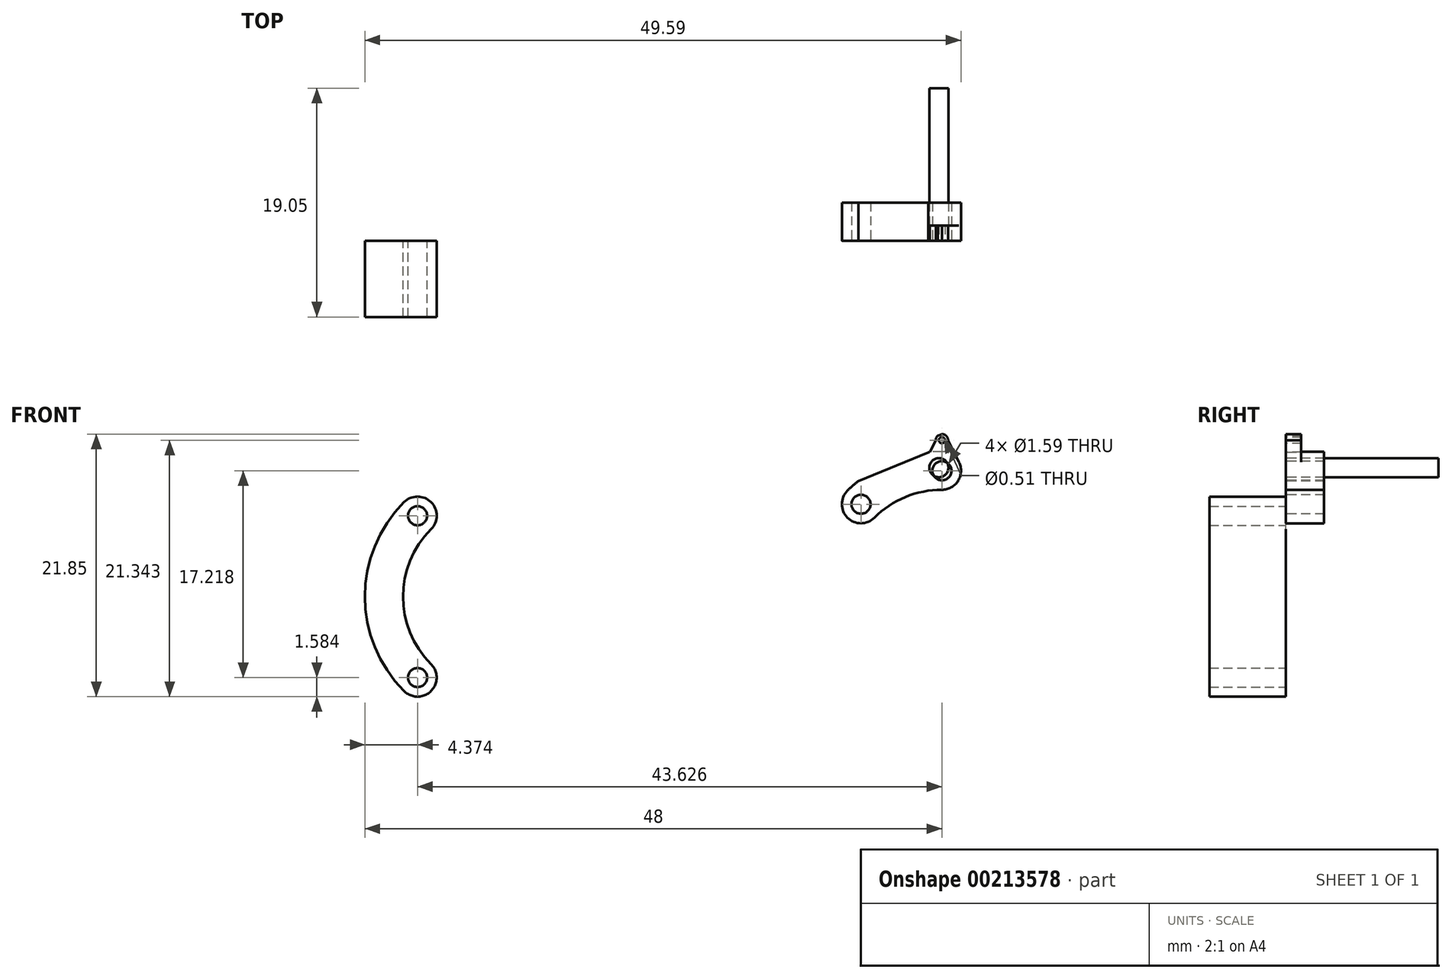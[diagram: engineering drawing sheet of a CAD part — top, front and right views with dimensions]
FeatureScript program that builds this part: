
annotation { "Feature Type Name" : "Feature", "Feature Type Description" : "" }
export const myFeature = defineFeature(function(context is Context, id is Id, definition is map)
    precondition{}
    {
        {
            var Q0;
            Q0=qCreatedBy(makeId("Front.planeOp"),FACE);
            var sketch = newSketch(context, id + "F0", { "sketchPlane" : qUnion([Q0])});
            skCircle(sketch, "E0", {"center": v(0, 0) * mm, "radius": 7.94 * mm});
            skCircle(sketch, "E1", {"center": v(0, 0) * mm, "radius": 11.11 * mm});
            skCircle(sketch, "E2", {"center": v(0, 0) * mm, "radius": 9.53 * mm, "construction": true});
            skLineSegment(sketch, "E3", {"start": v(0, 14.42) * mm, "end": v(0, -15.59) * mm, "construction": true});
            skLineSegment(sketch, "E4", {"start": v(-14.56, 0) * mm, "end": v(14.44, 0) * mm, "construction": true});
            skLineSegment(sketch, "E5", {"start": v(0, 0) * mm, "end": v(10.85, 10.85) * mm, "construction": true});
            skLineSegment(sketch, "E6", {"start": v(0, 0) * mm, "end": v(-10.67, -10.67) * mm, "construction": true});
            skLineSegment(sketch, "E7", {"start": v(0, 0) * mm, "end": v(-10.13, 10.13) * mm, "construction": true});
            skLineSegment(sketch, "E8", {"start": v(0, 0) * mm, "end": v(10, -10) * mm, "construction": true});
            skCircle(sketch, "E9", {"center": v(0, 9.53) * mm, "radius": 0.8 * mm});
            skCircle(sketch, "E10", {"center": v(-6.74, 6.74) * mm, "radius": 0.8 * mm});
            skCircle(sketch, "E11", {"center": v(-6.74, -6.74) * mm, "radius": 0.8 * mm});
            skCircle(sketch, "E12", {"center": v(6.74, -6.74) * mm, "radius": 0.8 * mm});
            skCircle(sketch, "E13", {"center": v(6.74, 6.74) * mm, "radius": 0.8 * mm});
            skCircle(sketch, "E14", {"center": v(0, -9.53) * mm, "radius": 0.8 * mm});
            skCircle(sketch, "E15", {"center": v(0, 9.53) * mm, "radius": 1.59 * mm});
            skCircle(sketch, "E16", {"center": v(-6.74, 6.74) * mm, "radius": 1.59 * mm});
            skCircle(sketch, "E17", {"center": v(-6.74, -6.74) * mm, "radius": 1.59 * mm});
            skCircle(sketch, "E18", {"center": v(0, -9.53) * mm, "radius": 1.59 * mm});
            skCircle(sketch, "E19", {"center": v(6.74, -6.74) * mm, "radius": 1.59 * mm});
            skCircle(sketch, "E20", {"center": v(6.74, 6.74) * mm, "radius": 1.59 * mm});
            skCircle(sketch, "E21", {"center": v(0, 12.07) * mm, "radius": 0.25 * mm});
            skCircle(sketch, "E22", {"center": v(-8.53, 8.53) * mm, "radius": 0.25 * mm});
            skCircle(sketch, "E23", {"center": v(-8.53, -8.53) * mm, "radius": 0.25 * mm});
            skCircle(sketch, "E24", {"center": v(0, -12.07) * mm, "radius": 0.25 * mm});
            skCircle(sketch, "E25", {"center": v(8.53, -8.53) * mm, "radius": 0.25 * mm});
            skCircle(sketch, "E26", {"center": v(8.53, 8.53) * mm, "radius": 0.25 * mm});
            skCircle(sketch, "E27", {"center": v(0, 12.07) * mm, "radius": 0.5 * mm});
            skCircle(sketch, "E28", {"center": v(-8.53, 8.53) * mm, "radius": 0.5 * mm});
            skCircle(sketch, "E29", {"center": v(8.53, 8.53) * mm, "radius": 0.5 * mm});
            skCircle(sketch, "E30", {"center": v(8.53, -8.53) * mm, "radius": 0.5 * mm});
            skCircle(sketch, "E31", {"center": v(0, -12.07) * mm, "radius": 0.5 * mm});
            skCircle(sketch, "E32", {"center": v(-8.53, -8.53) * mm, "radius": 0.5 * mm});
            skLineSegment(sketch, "E33", {"start": v(-0.5, 12.05) * mm, "end": v(-1.42, 10.24) * mm});
            skLineSegment(sketch, "E34", {"start": v(0.5, 12.05) * mm, "end": v(1.42, 10.24) * mm});
            skLineSegment(sketch, "E35", {"start": v(-8.88, 8.16) * mm, "end": v(-8.24, 6.23) * mm});
            skLineSegment(sketch, "E36", {"start": v(-8.16, 8.88) * mm, "end": v(-6.23, 8.24) * mm});
            skLineSegment(sketch, "E37", {"start": v(-8.88, -8.16) * mm, "end": v(-8.24, -6.23) * mm});
            skLineSegment(sketch, "E38", {"start": v(-8.16, -8.88) * mm, "end": v(-6.23, -8.24) * mm});
            skLineSegment(sketch, "E39", {"start": v(-0.5, -12.05) * mm, "end": v(-1.42, -10.24) * mm});
            skLineSegment(sketch, "E40", {"start": v(0.5, -12.05) * mm, "end": v(1.42, -10.24) * mm});
            skLineSegment(sketch, "E41", {"start": v(8.16, -8.88) * mm, "end": v(6.23, -8.24) * mm});
            skLineSegment(sketch, "E42", {"start": v(8.88, -8.16) * mm, "end": v(8.24, -6.23) * mm});
            skLineSegment(sketch, "E43", {"start": v(8.88, 8.16) * mm, "end": v(8.24, 6.23) * mm});
            skLineSegment(sketch, "E44", {"start": v(8.16, 8.88) * mm, "end": v(6.23, 8.24) * mm});
            skLineSegment(sketch, "E45", {"start": v(-8.17, 8.17) * mm, "end": v(0, 11.52) * mm});
            skLineSegment(sketch, "E46", {"start": v(0, 12.57) * mm, "end": v(-8.92, 8.92) * mm});
            skLineSegment(sketch, "E47", {"start": v(-8.92, 8.92) * mm, "end": v(-8.9, -8.9) * mm});
            skLineSegment(sketch, "E48", {"start": v(-8.17, 8.17) * mm, "end": v(-8.17, -8.17) * mm});
            skLineSegment(sketch, "E49", {"start": v(0, -12.57) * mm, "end": v(-8.9, -8.9) * mm});
            skLineSegment(sketch, "E50", {"start": v(0, -11.56) * mm, "end": v(-8.17, -8.17) * mm});
            skSolve(sketch);
        }
        {
            var Q0;
            Q0=qCreatedBy(makeId("Front.planeOp"),FACE);
            var sketch = newSketch(context, id + "F1", { "sketchPlane" : qUnion([Q0])});
            skCircle(sketch, "E51", {"center": v(0.25, -0.25) * mm, "radius": 7.94 * mm});
            skCircle(sketch, "E52", {"center": v(0.25, -0.25) * mm, "radius": 11.11 * mm});
            skCircle(sketch, "E53", {"center": v(0.25, -0.25) * mm, "radius": 9.53 * mm, "construction": true});
            skLineSegment(sketch, "E54", {"start": v(0.25, 14.16) * mm, "end": v(0.25, -15.84) * mm, "construction": true});
            skLineSegment(sketch, "E55", {"start": v(-14.31, -0.25) * mm, "end": v(14.69, -0.25) * mm, "construction": true});
            skLineSegment(sketch, "E56", {"start": v(0.25, -0.25) * mm, "end": v(11.1, 10.6) * mm, "construction": true});
            skLineSegment(sketch, "E57", {"start": v(0.25, -0.25) * mm, "end": v(-10.42, -10.93) * mm, "construction": true});
            skLineSegment(sketch, "E58", {"start": v(0.25, -0.25) * mm, "end": v(-9.88, 9.88) * mm, "construction": true});
            skLineSegment(sketch, "E59", {"start": v(0.25, -0.25) * mm, "end": v(10.24, -10.25) * mm, "construction": true});
            skCircle(sketch, "E60", {"center": v(0.25, 9.27) * mm, "radius": 0.8 * mm});
            skCircle(sketch, "E61", {"center": v(-6.49, 6.48) * mm, "radius": 0.8 * mm});
            skCircle(sketch, "E62", {"center": v(-6.49, -6.99) * mm, "radius": 0.8 * mm});
            skCircle(sketch, "E63", {"center": v(6.98, -6.99) * mm, "radius": 0.8 * mm});
            skCircle(sketch, "E64", {"center": v(6.98, 6.48) * mm, "radius": 0.8 * mm});
            skCircle(sketch, "E65", {"center": v(0.25, -9.78) * mm, "radius": 0.8 * mm});
            skCircle(sketch, "E66", {"center": v(0.25, 9.27) * mm, "radius": 1.59 * mm});
            skCircle(sketch, "E67", {"center": v(-6.49, 6.48) * mm, "radius": 1.59 * mm});
            skCircle(sketch, "E68", {"center": v(-6.49, -6.99) * mm, "radius": 1.59 * mm});
            skCircle(sketch, "E69", {"center": v(0.25, -9.78) * mm, "radius": 1.59 * mm});
            skCircle(sketch, "E70", {"center": v(6.98, -6.99) * mm, "radius": 1.59 * mm});
            skCircle(sketch, "E71", {"center": v(6.98, 6.48) * mm, "radius": 1.59 * mm});
            skCircle(sketch, "E72", {"center": v(0.25, 11.81) * mm, "radius": 0.25 * mm});
            skCircle(sketch, "E73", {"center": v(-8.28, 8.28) * mm, "radius": 0.25 * mm});
            skCircle(sketch, "E74", {"center": v(-8.28, -8.78) * mm, "radius": 0.25 * mm});
            skCircle(sketch, "E75", {"center": v(0.25, -12.32) * mm, "radius": 0.25 * mm});
            skCircle(sketch, "E76", {"center": v(8.78, -8.78) * mm, "radius": 0.25 * mm});
            skCircle(sketch, "E77", {"center": v(8.78, 8.28) * mm, "radius": 0.25 * mm});
            skCircle(sketch, "E78", {"center": v(0.25, 11.81) * mm, "radius": 0.5 * mm});
            skCircle(sketch, "E79", {"center": v(-8.28, 8.28) * mm, "radius": 0.5 * mm});
            skCircle(sketch, "E80", {"center": v(8.78, 8.28) * mm, "radius": 0.5 * mm});
            skCircle(sketch, "E81", {"center": v(8.78, -8.78) * mm, "radius": 0.5 * mm});
            skCircle(sketch, "E82", {"center": v(0.25, -12.32) * mm, "radius": 0.5 * mm});
            skCircle(sketch, "E83", {"center": v(-8.28, -8.78) * mm, "radius": 0.5 * mm});
            skLineSegment(sketch, "E84", {"start": v(-0.26, 11.8) * mm, "end": v(-1.17, 9.98) * mm});
            skLineSegment(sketch, "E85", {"start": v(0.76, 11.8) * mm, "end": v(1.67, 9.98) * mm});
            skLineSegment(sketch, "E86", {"start": v(-8.63, 7.91) * mm, "end": v(-8, 5.98) * mm});
            skLineSegment(sketch, "E87", {"start": v(-7.91, 8.63) * mm, "end": v(-5.99, 7.99) * mm});
            skLineSegment(sketch, "E88", {"start": v(-8.63, -8.42) * mm, "end": v(-8, -6.49) * mm});
            skLineSegment(sketch, "E89", {"start": v(-7.91, -9.14) * mm, "end": v(-5.99, -8.5) * mm});
            skLineSegment(sketch, "E90", {"start": v(-0.26, -12.3) * mm, "end": v(-1.17, -10.49) * mm});
            skLineSegment(sketch, "E91", {"start": v(0.76, -12.3) * mm, "end": v(1.67, -10.49) * mm});
            skLineSegment(sketch, "E92", {"start": v(8.41, -9.14) * mm, "end": v(6.48, -8.5) * mm});
            skLineSegment(sketch, "E93", {"start": v(9.13, -8.42) * mm, "end": v(8.5, -6.49) * mm});
            skLineSegment(sketch, "E94", {"start": v(9.13, 7.91) * mm, "end": v(8.5, 5.98) * mm});
            skLineSegment(sketch, "E95", {"start": v(8.41, 8.63) * mm, "end": v(6.48, 7.99) * mm});
            skLineSegment(sketch, "E96", {"start": v(-7.92, 7.92) * mm, "end": v(0.25, 11.26) * mm});
            skLineSegment(sketch, "E97", {"start": v(0.25, 12.32) * mm, "end": v(-8.67, 8.67) * mm});
            skLineSegment(sketch, "E98", {"start": v(-8.67, 8.67) * mm, "end": v(-8.64, -9.14) * mm});
            skLineSegment(sketch, "E99", {"start": v(-7.92, 7.92) * mm, "end": v(-7.92, -8.42) * mm});
            skLineSegment(sketch, "E100", {"start": v(0.25, -12.83) * mm, "end": v(-8.64, -9.14) * mm});
            skLineSegment(sketch, "E101", {"start": v(0.25, -11.8) * mm, "end": v(-7.92, -8.42) * mm});
            skSolve(sketch);
        }
        {
            var Q0;
            Q0=makeQuery(id+"F0.imprint","IMPRINT",FACE,{"disambiguationData":[TD([[makeQuery(id+"F0.imprint","IMPRINT",EDGE,{"derivedFrom":sQuery(id+"F0.wireOp",EDGE,"E9")}),1.0]])]});
            extrude(context, id + "F2", {"entities" : qUnion([Q0]), "oppositeDirection" : true, "depth" : 12.7 * mm});
        }
        {
            var Q0;
            Q0=makeQuery(id+"F1.imprint","IMPRINT",FACE,{"disambiguationData":[TD([[makeQuery(id+"F1.imprint","IMPRINT",EDGE,{"derivedFrom":sQuery(id+"F1.wireOp",EDGE,"E60")}),-1.0]])]});
            var Q1;
            {var subQ1=sQuery(id+"F1.wireOp",EDGE,"E66");var subQ3=sQuery(id+"F1.wireOp",EDGE,"E51");var subQ4=makeQuery(id+"F1.imprint","INTERSECT",VERTEX,{"derivedFrom":[subQ3,subQ1]});Q1=makeQuery(id+"F1.imprint","IMPRINT",FACE,{"disambiguationData":[TD([[makeQuery(id+"F1.imprint","IMPRINT",EDGE,{"disambiguationData":[TD([[subQ4,-1.0]])],"derivedFrom":subQ3}),-1.0]])]});}
            var Q2;
            {var subQ0=sQuery(id+"F1.wireOp",EDGE,"E66");var subQ1=sQuery(id+"F1.wireOp",EDGE,"E52");var subQ2=makeQuery(id+"F1.imprint","INTERSECT",VERTEX,{"derivedFrom":[subQ1,subQ0]});Q2=makeQuery(id+"F1.imprint","IMPRINT",FACE,{"disambiguationData":[TD([[makeQuery(id+"F1.imprint","IMPRINT",EDGE,{"disambiguationData":[TD([[subQ2,-1.0]])],"derivedFrom":subQ1}),1.0]])]});}
            var Q3;
            {var subQ0=sQuery(id+"F1.wireOp",EDGE,"E87");var subQ1=sQuery(id+"F1.wireOp",EDGE,"E52");var subQ2=makeQuery(id+"F1.imprint","INTERSECT",VERTEX,{"derivedFrom":[subQ1,subQ0]});Q3=makeQuery(id+"F1.imprint","IMPRINT",FACE,{"disambiguationData":[TD([[makeQuery(id+"F1.imprint","IMPRINT",EDGE,{"disambiguationData":[TD([[subQ2,-1.0]])],"derivedFrom":subQ1}),1.0]])]});}
            var Q4;
            Q4=makeQuery(id+"F1.imprint","IMPRINT",FACE,{"disambiguationData":[TD([[makeQuery(id+"F1.imprint","IMPRINT",EDGE,{"derivedFrom":sQuery(id+"F1.wireOp",EDGE,"E61")}),-1.0]])]});
            var Q5;
            {var subQ0=sQuery(id+"F1.wireOp",EDGE,"E67");var subQ1=makeQuery(id+"F1.imprint","INTERSECT",VERTEX,{"derivedFrom":[subQ0,sQuery(id+"F1.wireOp",EDGE,"E86")]});Q5=makeQuery(id+"F1.imprint","IMPRINT",FACE,{"disambiguationData":[TD([[makeQuery(id+"F1.imprint","IMPRINT",EDGE,{"disambiguationData":[TD([[subQ1,1.0]])],"derivedFrom":subQ0}),1.0]])]});}
            var Q6;
            {var subQ0=sQuery(id+"F1.wireOp",EDGE,"E96");var subQ1=sQuery(id+"F1.wireOp",EDGE,"E52");var subQ2=makeQuery(id+"F1.imprint","INTERSECT",VERTEX,{"disambiguationData":[OD(0.0)],"derivedFrom":[subQ1,subQ0]});Q6=makeQuery(id+"F1.imprint","IMPRINT",FACE,{"disambiguationData":[TD([[makeQuery(id+"F1.imprint","IMPRINT",EDGE,{"disambiguationData":[TD([[subQ2,-1.0]])],"derivedFrom":subQ1}),1.0]])]});}
            extrude(context, id + "F3", {"entities" : qUnion([Q0, Q1, Q2, Q3, Q4, Q5, Q6]), "oppositeDirection" : true, "depth" : 3.17 * mm});
        }
        {
            var Q0;
            {var subQ4=sQuery(id+"F1.wireOp",EDGE,"E85");var subQ5=sQuery(id+"F1.wireOp",EDGE,"E52");var subQ6=makeQuery(id+"F1.imprint","INTERSECT",VERTEX,{"derivedFrom":[subQ5,subQ4]});Q0=makeQuery(id+"F1.imprint","IMPRINT",FACE,{"disambiguationData":[TD([[makeQuery(id+"F1.imprint","IMPRINT",EDGE,{"disambiguationData":[TD([[subQ6,-1.0]])],"derivedFrom":subQ5}),-1.0]])]});}
            var Q1;
            Q1=makeQuery(id+"F1.imprint","IMPRINT",FACE,{"disambiguationData":[TD([[makeQuery(id+"F1.imprint","IMPRINT",EDGE,{"derivedFrom":sQuery(id+"F1.wireOp",EDGE,"E72")}),-1.0]])]});
            var Q2;
            {var subQ0=sQuery(id+"F1.wireOp",EDGE,"E85");var subQ1=sQuery(id+"F1.wireOp",EDGE,"E52");var subQ2=makeQuery(id+"F1.imprint","INTERSECT",VERTEX,{"derivedFrom":[subQ1,subQ0]});Q2=makeQuery(id+"F1.imprint","IMPRINT",FACE,{"disambiguationData":[TD([[makeQuery(id+"F1.imprint","IMPRINT",EDGE,{"disambiguationData":[TD([[subQ2,-1.0]])],"derivedFrom":subQ1}),1.0]])]});}
            var Q3;
            {var subQ0=sQuery(id+"F1.wireOp",EDGE,"E97");var subQ1=sQuery(id+"F1.wireOp",EDGE,"E78");var subQ2=makeQuery(id+"F1.imprint","INTERSECT",VERTEX,{"disambiguationData":[OD(0.0)],"derivedFrom":[subQ1,subQ0]});Q3=makeQuery(id+"F1.imprint","IMPRINT",FACE,{"disambiguationData":[TD([[makeQuery(id+"F1.imprint","IMPRINT",EDGE,{"disambiguationData":[TD([[subQ2,-1.0]])],"derivedFrom":subQ1}),1.0]])]});}
            extrude(context, id + "F4", {"entities" : qUnion([Q0, Q1, Q2, Q3]), "operationType" : NewBodyOperationType.ADD, "oppositeDirection" : true, "depth" : 1.27 * mm});
        }
        {
            var Q0;
            Q0=qCreatedBy(makeId("Front.planeOp"),FACE);
            var sketch = newSketch(context, id + "F5", { "sketchPlane" : qUnion([Q0])});
            skCircle(sketch, "E102", {"center": v(-36.64, -1.21) * mm, "radius": 7.94 * mm});
            skCircle(sketch, "E103", {"center": v(-36.64, -1.21) * mm, "radius": 11.11 * mm});
            skCircle(sketch, "E104", {"center": v(-36.64, -1.21) * mm, "radius": 9.53 * mm, "construction": true});
            skLineSegment(sketch, "E105", {"start": v(-36.64, 13.2) * mm, "end": v(-36.64, -16.8) * mm, "construction": true});
            skLineSegment(sketch, "E106", {"start": v(-51.2, -1.21) * mm, "end": v(-22.2, -1.21) * mm, "construction": true});
            skLineSegment(sketch, "E107", {"start": v(-36.64, -1.21) * mm, "end": v(-25.8, 9.64) * mm, "construction": true});
            skLineSegment(sketch, "E108", {"start": v(-36.64, -1.21) * mm, "end": v(-47.31, -11.88) * mm, "construction": true});
            skLineSegment(sketch, "E109", {"start": v(-36.64, -1.21) * mm, "end": v(-46.78, 8.92) * mm, "construction": true});
            skLineSegment(sketch, "E110", {"start": v(-36.64, -1.21) * mm, "end": v(-26.65, -11.2) * mm, "construction": true});
            skCircle(sketch, "E111", {"center": v(-36.64, 8.31) * mm, "radius": 0.8 * mm});
            skCircle(sketch, "E112", {"center": v(-43.38, 5.52) * mm, "radius": 0.8 * mm});
            skCircle(sketch, "E113", {"center": v(-43.38, -7.95) * mm, "radius": 0.8 * mm});
            skCircle(sketch, "E114", {"center": v(-29.9, -7.95) * mm, "radius": 0.8 * mm});
            skCircle(sketch, "E115", {"center": v(-29.9, 5.52) * mm, "radius": 0.8 * mm});
            skCircle(sketch, "E116", {"center": v(-36.64, -10.74) * mm, "radius": 0.8 * mm});
            skCircle(sketch, "E117", {"center": v(-36.64, 8.31) * mm, "radius": 1.59 * mm});
            skCircle(sketch, "E118", {"center": v(-43.38, 5.52) * mm, "radius": 1.59 * mm});
            skCircle(sketch, "E119", {"center": v(-43.38, -7.95) * mm, "radius": 1.59 * mm});
            skCircle(sketch, "E120", {"center": v(-36.64, -10.74) * mm, "radius": 1.59 * mm});
            skCircle(sketch, "E121", {"center": v(-29.9, -7.95) * mm, "radius": 1.59 * mm});
            skCircle(sketch, "E122", {"center": v(-29.9, 5.52) * mm, "radius": 1.59 * mm});
            skCircle(sketch, "E123", {"center": v(-36.64, 10.85) * mm, "radius": 0.25 * mm});
            skCircle(sketch, "E124", {"center": v(-45.17, 7.32) * mm, "radius": 0.25 * mm});
            skCircle(sketch, "E125", {"center": v(-45.17, -9.74) * mm, "radius": 0.25 * mm});
            skCircle(sketch, "E126", {"center": v(-36.64, -13.28) * mm, "radius": 0.25 * mm});
            skCircle(sketch, "E127", {"center": v(-28.1, -9.74) * mm, "radius": 0.25 * mm});
            skCircle(sketch, "E128", {"center": v(-28.1, 7.32) * mm, "radius": 0.25 * mm});
            skCircle(sketch, "E129", {"center": v(-36.64, 10.85) * mm, "radius": 0.5 * mm});
            skCircle(sketch, "E130", {"center": v(-45.17, 7.32) * mm, "radius": 0.5 * mm});
            skCircle(sketch, "E131", {"center": v(-28.1, 7.32) * mm, "radius": 0.5 * mm});
            skCircle(sketch, "E132", {"center": v(-28.1, -9.74) * mm, "radius": 0.5 * mm});
            skCircle(sketch, "E133", {"center": v(-36.64, -13.28) * mm, "radius": 0.5 * mm});
            skCircle(sketch, "E134", {"center": v(-45.17, -9.74) * mm, "radius": 0.5 * mm});
            skLineSegment(sketch, "E135", {"start": v(-37.15, 10.84) * mm, "end": v(-38.06, 9.03) * mm});
            skLineSegment(sketch, "E136", {"start": v(-36.13, 10.84) * mm, "end": v(-35.22, 9.03) * mm});
            skLineSegment(sketch, "E137", {"start": v(-45.52, 6.95) * mm, "end": v(-44.88, 5.02) * mm});
            skLineSegment(sketch, "E138", {"start": v(-44.8, 7.67) * mm, "end": v(-42.88, 7.03) * mm});
            skLineSegment(sketch, "E139", {"start": v(-45.52, -9.38) * mm, "end": v(-44.88, -7.45) * mm});
            skLineSegment(sketch, "E140", {"start": v(-44.8, -10.1) * mm, "end": v(-42.88, -9.45) * mm});
            skLineSegment(sketch, "E141", {"start": v(-37.15, -13.26) * mm, "end": v(-38.06, -11.45) * mm});
            skLineSegment(sketch, "E142", {"start": v(-36.13, -13.26) * mm, "end": v(-35.22, -11.45) * mm});
            skLineSegment(sketch, "E143", {"start": v(-28.48, -10.1) * mm, "end": v(-30.4, -9.45) * mm});
            skLineSegment(sketch, "E144", {"start": v(-27.76, -9.38) * mm, "end": v(-28.4, -7.45) * mm});
            skLineSegment(sketch, "E145", {"start": v(-27.76, 6.95) * mm, "end": v(-28.4, 5.02) * mm});
            skLineSegment(sketch, "E146", {"start": v(-28.48, 7.67) * mm, "end": v(-30.4, 7.03) * mm});
            skLineSegment(sketch, "E147", {"start": v(-44.81, 6.96) * mm, "end": v(-36.64, 10.3) * mm});
            skLineSegment(sketch, "E148", {"start": v(-36.64, 11.36) * mm, "end": v(-45.56, 7.71) * mm});
            skLineSegment(sketch, "E149", {"start": v(-45.56, 7.71) * mm, "end": v(-45.53, -10.1) * mm});
            skLineSegment(sketch, "E150", {"start": v(-44.81, 6.96) * mm, "end": v(-44.81, -9.38) * mm});
            skLineSegment(sketch, "E151", {"start": v(-36.64, -13.78) * mm, "end": v(-45.53, -10.1) * mm});
            skLineSegment(sketch, "E152", {"start": v(-36.64, -12.77) * mm, "end": v(-44.81, -9.38) * mm});
            skSolve(sketch);
        }
        {
            var Q0;
            Q0=makeQuery(id+"F5.imprint","IMPRINT",FACE,{"disambiguationData":[TD([[makeQuery(id+"F5.imprint","IMPRINT",EDGE,{"derivedFrom":sQuery(id+"F5.wireOp",EDGE,"E112")}),-1.0]])]});
            var Q1;
            {var subQ0=sQuery(id+"F5.wireOp",EDGE,"E118");var subQ1=makeQuery(id+"F5.imprint","INTERSECT",VERTEX,{"derivedFrom":[subQ0,sQuery(id+"F5.wireOp",EDGE,"E137")]});Q1=makeQuery(id+"F5.imprint","IMPRINT",FACE,{"disambiguationData":[TD([[makeQuery(id+"F5.imprint","IMPRINT",EDGE,{"disambiguationData":[TD([[subQ1,1.0]])],"derivedFrom":subQ0}),1.0]])]});}
            var Q2;
            {var subQ0=sQuery(id+"F5.wireOp",EDGE,"E150");var subQ1=sQuery(id+"F5.wireOp",EDGE,"E103");var subQ2=makeQuery(id+"F5.imprint","INTERSECT",VERTEX,{"disambiguationData":[OD(0.0)],"derivedFrom":[subQ1,subQ0]});Q2=makeQuery(id+"F5.imprint","IMPRINT",FACE,{"disambiguationData":[TD([[makeQuery(id+"F5.imprint","IMPRINT",EDGE,{"disambiguationData":[TD([[subQ2,-1.0]])],"derivedFrom":subQ1}),1.0]])]});}
            var Q3;
            {var subQ9=sQuery(id+"F5.wireOp",EDGE,"E103");var subQ11=sQuery(id+"F5.wireOp",EDGE,"E149");var subQ13=makeQuery(id+"F5.imprint","INTERSECT",VERTEX,{"disambiguationData":[OD(0.0)],"derivedFrom":[subQ9,subQ11]});Q3=makeQuery(id+"F5.imprint","IMPRINT",FACE,{"disambiguationData":[TD([[makeQuery(id+"F5.imprint","IMPRINT",EDGE,{"disambiguationData":[TD([[subQ13,1.0]])],"derivedFrom":subQ9}),1.0]])]});}
            var Q4;
            {var subQ0=sQuery(id+"F5.wireOp",EDGE,"E149");var subQ1=sQuery(id+"F5.wireOp",EDGE,"E103");var subQ2=makeQuery(id+"F5.imprint","INTERSECT",VERTEX,{"disambiguationData":[OD(0.0)],"derivedFrom":[subQ1,subQ0]});Q4=makeQuery(id+"F5.imprint","IMPRINT",FACE,{"disambiguationData":[TD([[makeQuery(id+"F5.imprint","IMPRINT",EDGE,{"disambiguationData":[TD([[subQ2,-1.0]])],"derivedFrom":subQ1}),1.0]])]});}
            var Q5;
            {var subQ0=sQuery(id+"F5.wireOp",EDGE,"E118");var subQ1=sQuery(id+"F5.wireOp",EDGE,"E102");var subQ2=makeQuery(id+"F5.imprint","INTERSECT",VERTEX,{"derivedFrom":[subQ1,subQ0]});Q5=makeQuery(id+"F5.imprint","IMPRINT",FACE,{"disambiguationData":[TD([[makeQuery(id+"F5.imprint","IMPRINT",EDGE,{"disambiguationData":[TD([[subQ2,-1.0]])],"derivedFrom":subQ1}),-1.0]])]});}
            var Q6;
            {var subQ0=sQuery(id+"F5.wireOp",EDGE,"E118");var subQ1=sQuery(id+"F5.wireOp",EDGE,"E103");var subQ2=makeQuery(id+"F5.imprint","INTERSECT",VERTEX,{"derivedFrom":[subQ1,subQ0]});Q6=makeQuery(id+"F5.imprint","IMPRINT",FACE,{"disambiguationData":[TD([[makeQuery(id+"F5.imprint","IMPRINT",EDGE,{"disambiguationData":[TD([[subQ2,-1.0]])],"derivedFrom":subQ1}),1.0]])]});}
            var Q7;
            Q7=makeQuery(id+"F5.imprint","IMPRINT",FACE,{"disambiguationData":[TD([[makeQuery(id+"F5.imprint","IMPRINT",EDGE,{"derivedFrom":sQuery(id+"F5.wireOp",EDGE,"E113")}),-1.0]])]});
            var Q8;
            {var subQ0=sQuery(id+"F5.wireOp",EDGE,"E119");var subQ1=makeQuery(id+"F5.imprint","INTERSECT",VERTEX,{"derivedFrom":[subQ0,sQuery(id+"F5.wireOp",EDGE,"E139")]});Q8=makeQuery(id+"F5.imprint","IMPRINT",FACE,{"disambiguationData":[TD([[makeQuery(id+"F5.imprint","IMPRINT",EDGE,{"disambiguationData":[TD([[subQ1,1.0]])],"derivedFrom":subQ0}),1.0]])]});}
            var Q9;
            {var subQ0=sQuery(id+"F5.wireOp",EDGE,"E139");var subQ1=sQuery(id+"F5.wireOp",EDGE,"E103");var subQ2=makeQuery(id+"F5.imprint","INTERSECT",VERTEX,{"derivedFrom":[subQ1,subQ0]});Q9=makeQuery(id+"F5.imprint","IMPRINT",FACE,{"disambiguationData":[TD([[makeQuery(id+"F5.imprint","IMPRINT",EDGE,{"disambiguationData":[TD([[subQ2,-1.0]])],"derivedFrom":subQ1}),1.0]])]});}
            var Q10;
            {var subQ0=sQuery(id+"F5.wireOp",EDGE,"E150");var subQ1=sQuery(id+"F5.wireOp",EDGE,"E103");var subQ2=makeQuery(id+"F5.imprint","INTERSECT",VERTEX,{"disambiguationData":[OD(1.0)],"derivedFrom":[subQ1,subQ0]});Q10=makeQuery(id+"F5.imprint","IMPRINT",FACE,{"disambiguationData":[TD([[makeQuery(id+"F5.imprint","IMPRINT",EDGE,{"disambiguationData":[TD([[subQ2,-1.0]])],"derivedFrom":subQ1}),1.0]])]});}
            extrude(context, id + "F6", {"entities" : qUnion([Q0, Q1, Q2, Q3, Q4, Q5, Q6, Q7, Q8, Q9, Q10]), "depth" : 6.35 * mm});
        }
    });
